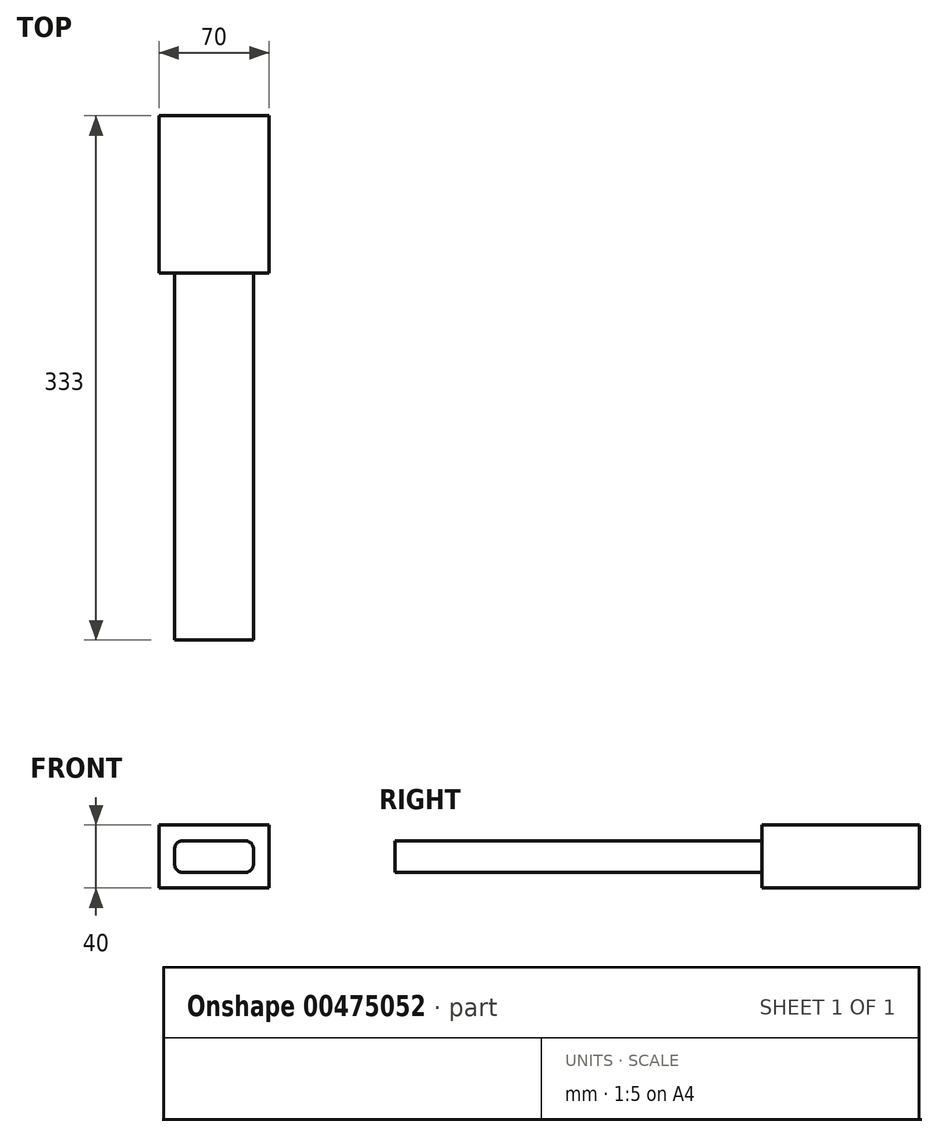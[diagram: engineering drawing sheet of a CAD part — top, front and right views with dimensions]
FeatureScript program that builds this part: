
annotation { "Feature Type Name" : "Feature", "Feature Type Description" : "" }
export const myFeature = defineFeature(function(context is Context, id is Id, definition is map)
    precondition{}
    {
        {
            var Q0;
            Q0=qCreatedBy(makeId("Front.planeOp"),FACE);
            cPlane(context, id + "F0", {"entities" : qUnion([Q0]), "cplaneType" : CPlaneType.OFFSET, "offset" : 100 * mm, "oppositeDirection" : true, "width" : 150 * mm, "height" : 150 * mm});
        }
        {
            var Q0;
            Q0=qCreatedBy(makeId("Front.planeOp"),FACE);
            var sketch = newSketch(context, id + "F1", { "sketchPlane" : qUnion([Q0])});
            skLineSegment(sketch, "E0.bottom", {"start": v(-50, 20) * mm, "end": v(0, 20) * mm});
            skLineSegment(sketch, "E0.top", {"start": v(-50, 0) * mm, "end": v(0, 0) * mm});
            skLineSegment(sketch, "E0.left", {"start": v(-50, 20) * mm, "end": v(-50, 0) * mm});
            skLineSegment(sketch, "E0.right", {"start": v(0, 20) * mm, "end": v(0, 0) * mm});
            skSolve(sketch);
        }
        {
            var Q0;
            Q0 = qSketchRegion(id + "F1", true);
            extrude(context, id + "F2", {"entities" : qUnion([Q0]), "depth" : 233 * mm});
        }
        {
            var Q0;
            Q0=makeQuery(id+"F2.opExtrude","SWEPT_EDGE",EDGE,{"disambiguationData":[OSD([sQuery(id+"F1.wireOp",EDGE,"E0.bottom"),sQuery(id+"F1.wireOp",EDGE,"E0.left")])]});
            var Q1;
            Q1=makeQuery(id+"F2.opExtrude","SWEPT_EDGE",EDGE,{"disambiguationData":[OSD([sQuery(id+"F1.wireOp",EDGE,"E0.bottom"),sQuery(id+"F1.wireOp",EDGE,"E0.right")])]});
            var Q2;
            Q2=makeQuery(id+"F2.opExtrude","SWEPT_EDGE",EDGE,{"disambiguationData":[OSD([sQuery(id+"F1.wireOp",EDGE,"E0.top"),sQuery(id+"F1.wireOp",EDGE,"E0.left")])]});
            var Q3;
            Q3=makeQuery(id+"F2.opExtrude","SWEPT_EDGE",EDGE,{"disambiguationData":[OSD([sQuery(id+"F1.wireOp",EDGE,"E0.top"),sQuery(id+"F1.wireOp",EDGE,"E0.right")])]});
            fillet(context, id + "F3", {"entities" : qUnion([Q0, Q1, Q2, Q3]), "radius" : 5 * mm, "tangentPropagation" : true, "allowEdgeOverflow" : false});
        }
        {
            var Q0;
            Q0=qCreatedBy(id+"F0.planeOp",FACE);
            var sketch = newSketch(context, id + "F4", { "sketchPlane" : qUnion([Q0])});
            skLineSegment(sketch, "E1.bottom", {"start": v(-60, -10) * mm, "end": v(10, -10) * mm});
            skLineSegment(sketch, "E1.top", {"start": v(-60, 30) * mm, "end": v(10, 30) * mm});
            skLineSegment(sketch, "E1.left", {"start": v(-60, -10) * mm, "end": v(-60, 30) * mm});
            skLineSegment(sketch, "E1.right", {"start": v(10, -10) * mm, "end": v(10, 30) * mm});
            skSolve(sketch);
        }
        {
            var Q0;
            Q0 = qSketchRegion(id + "F4", true);
            var Q1;
            Q1=makeQuery(id+"F2.opExtrude","CAP_FACE",FACE,{"disambiguationData":[OSD([sQuery(id+"F1.wireOp",EDGE,"E0.bottom"),sQuery(id+"F1.wireOp",EDGE,"E0.top"),sQuery(id+"F1.wireOp",EDGE,"E0.left"),sQuery(id+"F1.wireOp",EDGE,"E0.right")])],"isStart":true});
            extrude(context, id + "F5", {"entities" : qUnion([Q0]), "endBound" : BoundingType.UP_TO_SURFACE, "endBoundEntityFace" : qUnion([Q1]), "depth" : 7 * mm});
        }
    });
